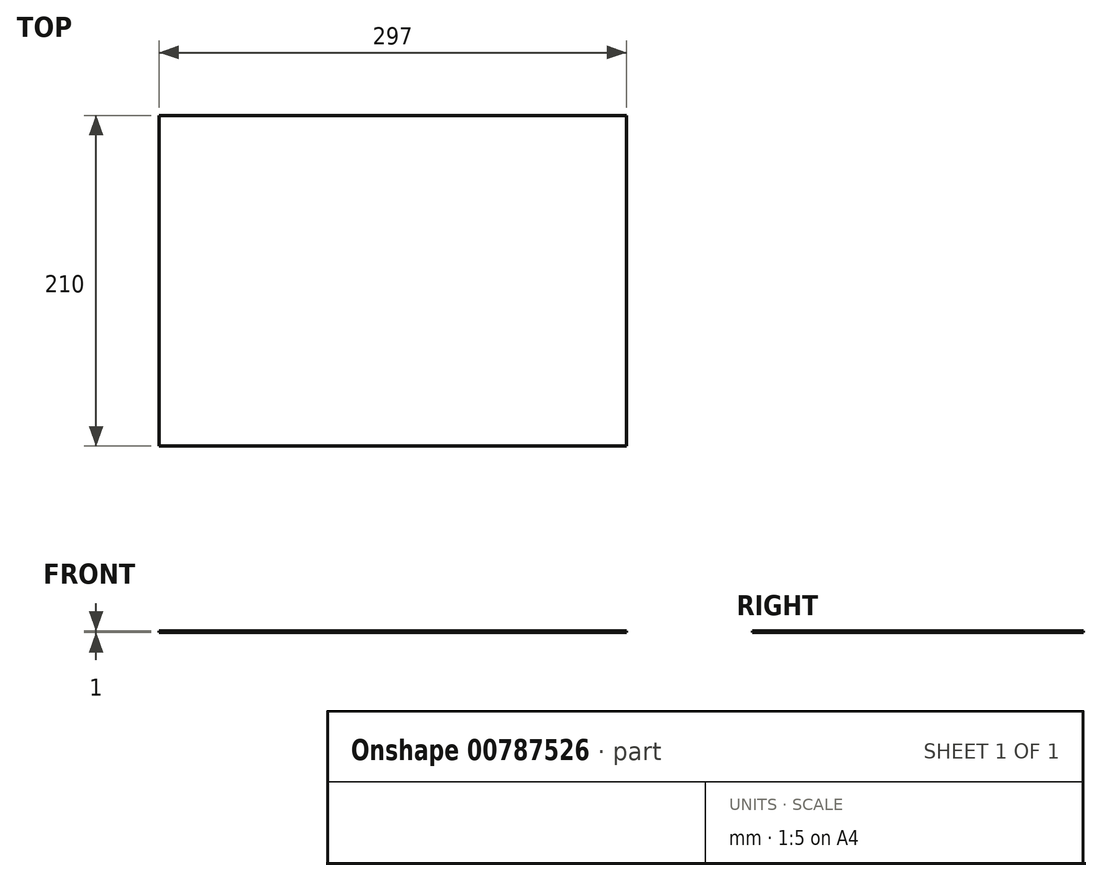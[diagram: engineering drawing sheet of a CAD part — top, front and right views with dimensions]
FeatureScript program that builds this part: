
annotation { "Feature Type Name" : "Feature", "Feature Type Description" : "" }
export const myFeature = defineFeature(function(context is Context, id is Id, definition is map)
    precondition{}
    {
        {
            var Q0;
            Q0=qCreatedBy(makeId("Top.planeOp"),FACE);
            var sketch = newSketch(context, id + "F0", { "sketchPlane" : qUnion([Q0])});
            skLineSegment(sketch, "E0.bottom", {"start": v(-148.5, 105) * mm, "end": v(148.5, 105) * mm});
            skLineSegment(sketch, "E0.top", {"start": v(-148.5, -105) * mm, "end": v(148.5, -105) * mm});
            skLineSegment(sketch, "E0.left", {"start": v(-148.5, 105) * mm, "end": v(-148.5, -105) * mm});
            skLineSegment(sketch, "E0.right", {"start": v(148.5, 105) * mm, "end": v(148.5, -105) * mm});
            skPoint(sketch, "E0.middle", {"position": v(0, 0) * mm});
            skSolve(sketch);
        }
        {
            var Q0;
            Q0=makeQuery(id+"F0.imprint","IMPRINT",FACE,{"disambiguationData":[TD([[makeQuery(id+"F0.imprint","IMPRINT",EDGE,{"derivedFrom":sQuery(id+"F0.wireOp",EDGE,"E0.bottom")}),-1.0]])]});
            extrude(context, id + "F1", {"entities" : qUnion([Q0]), "depth" : 1 * mm, "offsetDistance" : 25.4 * mm});
        }
    });
